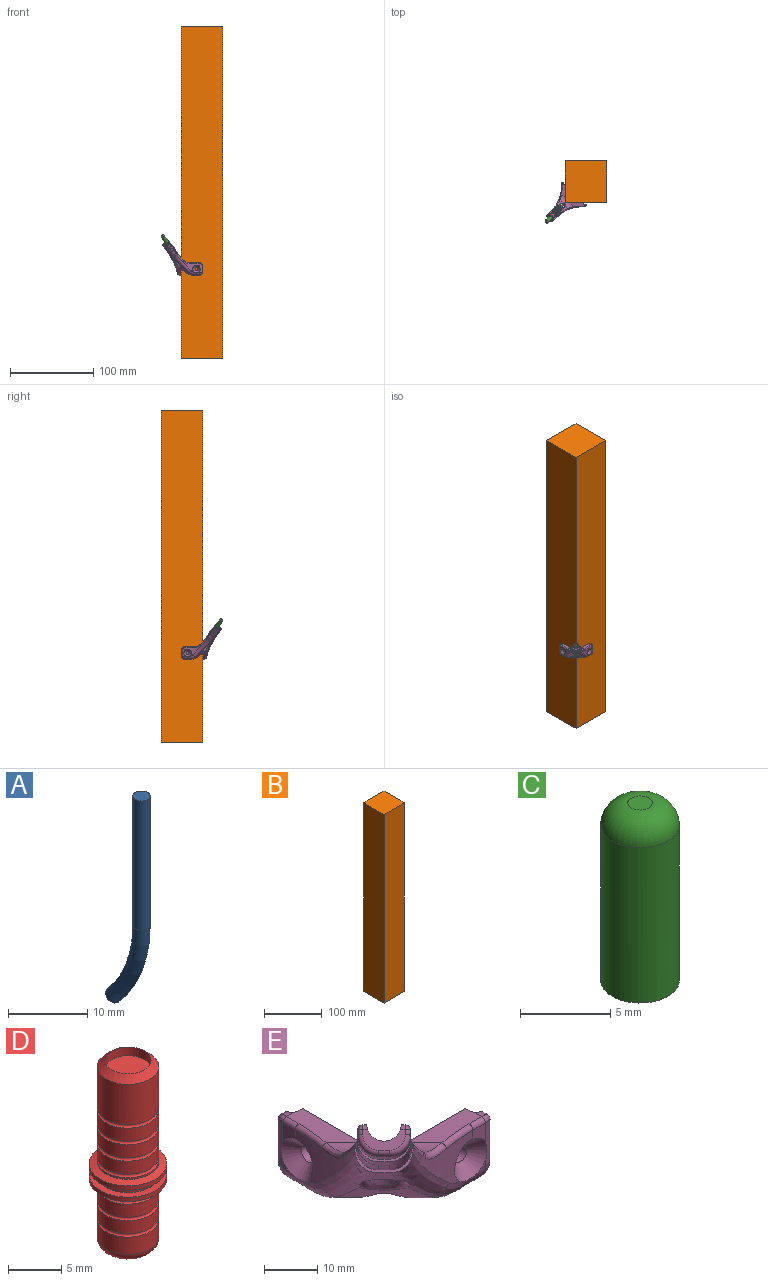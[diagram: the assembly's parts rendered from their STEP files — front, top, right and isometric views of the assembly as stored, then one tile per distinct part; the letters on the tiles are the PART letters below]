
ASSEMBLY  parts=5 mates=6
PART A: 4 faces, bbox 2.2x8.7x35.1 mm
  f0: plane 2.2x2.2mm, normal (0,0,1), area 3.8mm2, adj f2
  f1: plane 2.2x1.65mm, normal (0,0.66,-0.75), area 3.8mm2, adj f3
  f2: cylinder r=1.1mm len=20mm, axis (0,0,-1), area 138.2mm2, adj f0,f3
  f3: torus R=20mm, axis (1,0,0), area 99.9mm2, adj f1,f2
PART B: 6 faces, bbox 50x50x400 mm
  f0: plane 400x50mm, normal (0,-1,0), area 20000mm2, adj f1,f3,f4,f5
  f1: plane 400x50mm, normal (1,0,0), area 20000mm2, adj f0,f2,f4,f5
  f2: plane 400x50mm, normal (0,1,0), area 20000mm2, adj f1,f3,f4,f5
  f3: plane 400x50mm, normal (-1,0,0), area 20000mm2, adj f0,f2,f4,f5
  f4: plane 50x50mm, normal (0,0,1), area 2500mm2, adj f0,f1,f2,f3
  f5: plane 50x50mm, normal (0,0,-1), area 2500mm2, adj f0,f1,f2,f3
PART C: 4 faces, bbox 4.4x4.4x12 mm
  f0: cylinder r=2.17mm len=10.5mm, axis (0,0,-1), area 143.5mm2, adj f2,f3
  f1: plane 1.35x1.35mm, normal (0,0,1), area 1.4mm2, adj f3
  f2: plane 4.35x4.35mm, normal (0,0,-1), area 14.9mm2, adj f0
  f3: torus R=0.68mm, axis (0,0,1), area 24.1mm2, adj f0,f1
PART D: 30 faces, bbox 7.3x7.3x21.3 mm
  f0: cylinder r=2.9mm len=5.8mm, axis (0,0,-1), area 3.6mm2, adj f2,f10
  f1: cylinder r=2.9mm len=5.8mm, axis (0,0,-1), area 3.6mm2, adj f8,f9
  f2: cone r=2.9mm half-angle=73.3deg, axis (0,0,1), area 16.1mm2, adj f0,f3
  f3: cylinder r=3.65mm len=7.3mm, axis (0,0,-1), area 11.5mm2, adj f2,f4
  f4: plane 7.3x7.3mm, normal (0,0,1), area 15.4mm2, adj f3,f5
  f5: cylinder r=2.9mm len=5.8mm, axis (0,0,-1), area 14.6mm2, adj f4,f6
  f6: plane 7.3x7.3mm, normal (0,0,-1), area 15.4mm2, adj f5,f7
  f7: cylinder r=3.65mm len=7.3mm, axis (0,0,-1), area 11.5mm2, adj f6,f8
  f8: cone r=3.65mm half-angle=73.3deg, axis (0,0,-1), area 16.1mm2, adj f1,f7
  f9: torus R=2.9mm, axis (0,0,1), area 10.9mm2, adj f1,f11
  f10: torus R=2.9mm, axis (0,0,1), area 10.9mm2, adj f0,f13
  f11: cylinder r=2.9mm len=5.8mm, axis (0,0,-1), area 27.3mm2, adj f9,f12
  f12: torus R=2.9mm, axis (0,0,1), area 10.9mm2, adj f11,f15
  f13: cylinder r=2.9mm len=5.8mm, axis (0,0,-1), area 27.3mm2, adj f10,f14
  f14: torus R=2.9mm, axis (0,0,1), area 10.9mm2, adj f13,f23
  f15: cylinder r=2.9mm len=5.8mm, axis (0,0,-1), area 27.3mm2, adj f12,f16
  f16: torus R=2.9mm, axis (0,0,1), area 10.9mm2, adj f15,f17
  f17: cylinder r=2.9mm len=5.8mm, axis (0,0,-1), area 27.3mm2, adj f16,f18
  f18: torus R=2.9mm, axis (0,0,1), area 10.9mm2, adj f17,f22
  f19: plane 4.35x4.35mm, normal (0,0,1), area 14.9mm2, adj f20
  f20: cylinder r=2.17mm len=4.35mm, axis (0,0,1), area 13.7mm2, adj f19,f21
  f21: cone r=2.9mm half-angle=45deg, axis (0,0,-1), area 16.3mm2, adj f20,f22
  f22: cylinder r=2.9mm len=5.8mm, axis (0,0,-1), area 84.3mm2, adj f18,f21
  f23: cylinder r=2.9mm len=5.8mm, axis (0,0,-1), area 27.3mm2, adj f14,f24
  f24: torus R=2.9mm, axis (0,0,1), area 10.9mm2, adj f23,f26
  f25: plane 3.8x3.8mm, normal (0,0,-1), area 6.4mm2, adj f27,f28
  f26: cylinder r=2.9mm len=5.8mm, axis (0,0,-1), area 36.4mm2, adj f24,f27
  f27: torus R=1.9mm, axis (0,0,-1), area 25mm2, adj f25,f26
  f28: cylinder r=1.25mm len=3mm, axis (0,0,-1), area 23.6mm2, adj f25,f29
  f29: plane 2.5x2.5mm, normal (0,0,-1), area 4.9mm2, adj f28
PART E: 96 faces, bbox 50.5x50.5x41 mm
  f0: cylinder r=3mm len=10mm, axis (0,0,-1), area 35.9mm2, adj f27,f28,f71,f72,f73,f95
  f1: cylinder r=3mm len=2.91mm, axis (1,0,0), area 4.6mm2, adj f2,f37,f88,f91,f92,f93
  f2: bspline ~3.11x2.67mm, area 4.9mm2, adj f1,f30,f51,f92
  f3: cylinder r=1.25mm len=14.99mm, axis (0,0,1), area 40.8mm2, adj f4,f6,f70,f72,f87,f94
  f4: cylinder r=4mm len=4mm, axis (1,0,0), area 19.8mm2, adj f3,f5,f21,f28,f72,f73,f87
  f5: plane 6.68x1.07mm, normal (0,0,-1), area 6.2mm2, adj f4,f21,f38,f41,f87
  f6: plane 16.14x4.79mm, normal (0,0,1), area 58.5mm2, adj f3,f34,f38,f55,f56,f70,f87
  f7: plane 20.85x16.08mm, normal (1,0,0), area 270.2mm2, adj f20,f34,f36,f37,f42,f68,f76,f89
  f8: plane 6.92x6.92mm, normal (-0.5,-0.5,-0.71), area 28.8mm2, adj f13,f14,f80,f86
  f9: cylinder r=40mm len=24.02mm, axis (0,0,-1), area 92mm2, adj f13,f16,f22,f27,f56,f57,f78,f86
  f10: cylinder r=40mm len=5.65mm, axis (0,0,-1), area 6.9mm2, adj f16,f40,f49,f84,f85
  f11: cylinder r=40mm len=24.02mm, axis (0,0,-1), area 92mm2, adj f14,f15,f24,f25,f52,f53,f77,f86
  f12: cylinder r=40mm len=5.65mm, axis (0,0,-1), area 6.9mm2, adj f15,f39,f50,f84,f85
  f13: bspline ~21.97x21.5mm, area 143.1mm2, adj f8,f9,f20,f22,f80,f86
  f14: bspline ~21.97x21.5mm, area 143.1mm2, adj f8,f11,f20,f24,f80,f86
  f15: bspline ~15.71x12.85mm, area 35.9mm2, adj f11,f12,f33,f53,f54,f85,f86
  f16: bspline ~15.71x12.85mm, area 35.9mm2, adj f9,f10,f32,f57,f58,f85,f86
  f17: plane 6.36x6.03mm, normal (-0.5,-0.5,-0.71), area 18.6mm2, adj f18,f19,f49,f50,f82,f84
  f18: cylinder r=4mm len=9.65mm, axis (-0.5,-0.5,0.71), area 42.5mm2, adj f17,f31,f40,f49,f62,f81,f82,f83
  f19: cylinder r=4mm len=9.65mm, axis (0.5,0.5,-0.71), area 42.5mm2, adj f17,f31,f39,f50,f64,f81,f82,f83
  f20: plane 15.74x15.74mm, normal (-0.5,-0.5,-0.71), area 101.7mm2, adj f7,f13,f14,f38,f41,f42,f68,f80
  f21: torus R=44mm, axis (0,0,1), area 12.8mm2, adj f4,f5,f22,f73,f78
  f22: bspline ~10.48x7.01mm, area 37.5mm2, adj f9,f13,f21,f41,f78
  f23: torus R=44mm, axis (0,0,1), area 12.8mm2, adj f24,f29,f36,f75,f77
  f24: bspline ~10.95x7.07mm, area 37.5mm2, adj f11,f14,f23,f42,f77
  f25: plane 4.44x3.36mm, normal (-1,0,0), area 9.5mm2, adj f11,f30,f51,f75
  f26: plane 1.44x1.17mm, normal (-1,0,0), area 0.7mm2, adj f29,f30,f75
  f27: plane 4.44x3.36mm, normal (0,-1,0), area 9.5mm2, adj f0,f9,f55,f73
  f28: plane 1.44x1.17mm, normal (0,-1,0), area 0.7mm2, adj f0,f4,f73
  f29: cylinder r=4mm len=4mm, axis (0,-1,0), area 19.8mm2, adj f23,f26,f36,f69,f75,f88,f89
  f30: cylinder r=3mm len=10mm, axis (0,0,-1), area 35.5mm2, adj f2,f25,f26,f69,f75,f92
  f31: plane 2.91x2.91mm, normal (-0.5,-0.5,-0.71), area 6mm2, adj f18,f19,f63,f83
  f32: plane 21.26x17.62mm, normal (0.5,0.5,0.71), area 41.7mm2, adj f16,f34,f43,f44,f45,f46,f47,f48
  f33: plane 21.26x17.62mm, normal (0.5,0.5,0.71), area 41.7mm2, adj f15,f34,f43,f44,f45,f46,f47,f48
  f34: cylinder r=10mm len=20.43mm, axis (0.71,-0.71,0), area 119.8mm2, adj f6,f7,f32,f33,f37,f38,f48,f53
  f35: plane 6.63x6.63mm, normal (-0.5,-0.5,0.71), area 17.9mm2, adj f43,f59,f61,f62,f63,f64,f65,f67
  f36: plane 6.68x1.07mm, normal (0,0,-1), area 6.2mm2, adj f7,f23,f29,f42,f89
  f37: plane 16.14x4.79mm, normal (0,0,1), area 58.5mm2, adj f1,f7,f34,f51,f52,f88,f89
  f38: plane 20.85x16.08mm, normal (0,1,0), area 270.2mm2, adj f5,f6,f20,f34,f41,f68,f74,f87
  f39: plane 7.52x4.82mm, normal (-0.71,0.71,0), area 9.1mm2, adj f12,f19,f54,f65
  f40: plane 7.52x4.82mm, normal (0.71,-0.71,0), area 9.1mm2, adj f10,f18,f58,f61
  f41: cylinder r=10mm len=11.07mm, axis (0.71,-0.71,0), area 26.5mm2, adj f5,f20,f22,f38
  f42: cylinder r=10mm len=11.07mm, axis (0.71,-0.71,0), area 26.5mm2, adj f7,f20,f24,f36
  f43: cylinder r=3.25mm len=10.61mm, axis (-0.5,-0.5,0.71), area 111.3mm2, adj f32,f33,f35,f46,f59,f67
  f44: cylinder r=3.75mm len=7.15mm, axis (-0.5,-0.5,0.71), area 29.5mm2, adj f32,f33,f45,f46
  f45: plane 5.9x5.9mm, normal (-0.5,-0.5,0.71), area 5.5mm2, adj f32,f33,f44,f47
  f46: plane 5.9x5.9mm, normal (0.5,0.5,-0.71), area 5.5mm2, adj f32,f33,f43,f44
  f47: cylinder r=3.25mm len=12.9mm, axis (-0.5,-0.5,0.71), area 153.2mm2, adj f32,f33,f45,f79
  f48: extruded ~9.96x5.62mm, area 75.6mm2, adj f32,f33,f34,f79,f80
  f49: bspline ~18.12x15.11mm, area 32.9mm2, adj f10,f17,f18,f84
  f50: bspline ~18.12x15.11mm, area 32.9mm2, adj f12,f17,f19,f84
  f51: cylinder r=1mm len=3.36mm, axis (0,1,0), area 5.3mm2, adj f2,f25,f37,f52
  f52: torus R=41mm, axis (0,0,1), area 12.4mm2, adj f11,f37,f51,f53
  f53: bspline ~11.37x5.78mm, area 15.5mm2, adj f11,f15,f34,f52
  f54: cylinder r=1mm len=6.82mm, axis (-0.5,-0.5,0.71), area 13.6mm2, adj f15,f33,f39,f66
  f55: cylinder r=1mm len=3.36mm, axis (-1,0,0), area 5.3mm2, adj f6,f27,f56,f71
  f56: torus R=41mm, axis (0,0,1), area 12.4mm2, adj f6,f9,f55,f57
  f57: bspline ~11.37x5.78mm, area 15.5mm2, adj f9,f16,f34,f56
  f58: cylinder r=1mm len=6.82mm, axis (0.5,0.5,-0.71), area 13.6mm2, adj f16,f32,f40,f60
  f59: cylinder r=1mm len=1.64mm, axis (0.71,-0.71,0), area 1.3mm2, adj f32,f35,f43,f60
  f60: sphere r=1mm, area 1mm2, adj f58,f59,f61
  f61: cylinder r=1mm len=1.71mm, axis (0.5,0.5,0.71), area 1.6mm2, adj f35,f40,f60,f62
  f62: torus R=3mm, axis (0.5,0.5,-0.71), area 9mm2, adj f18,f35,f61,f63
  f63: cylinder r=1mm len=1.62mm, axis (0.71,-0.71,0), area 3.1mm2, adj f31,f35,f62,f64
  f64: torus R=3mm, axis (0.5,0.5,-0.71), area 9mm2, adj f19,f35,f63,f65
  f65: cylinder r=1mm len=1.71mm, axis (-0.5,-0.5,-0.71), area 1.6mm2, adj f35,f39,f64,f66
  f66: sphere r=1mm, area 1.6mm2, adj f54,f65,f67
  f67: cylinder r=1mm len=1.64mm, axis (0.71,-0.71,0), area 1.3mm2, adj f33,f35,f43,f66
  f68: cylinder r=1.5mm len=10.03mm, axis (0,0,1), area 23.6mm2, adj f7,f20,f34,f38
  f69: torus R=1mm, axis (0,1,0), area 14.8mm2, adj f29,f30,f88,f91,f92,f93
  f70: cylinder r=3mm len=2.91mm, axis (0,-1,0), area 4.6mm2, adj f3,f6,f71,f90,f94,f95
  f71: bspline ~3.11x2.67mm, area 4.9mm2, adj f0,f55,f70,f95
  f72: torus R=1mm, axis (1,0,0), area 14.8mm2, adj f0,f3,f4,f90,f94,f95
  f73: cone r=1.8mm half-angle=45deg, axis (0,-1,0), area 75.2mm2, adj f0,f4,f21,f27,f28,f74,f78
  f74: cylinder r=1.8mm len=3.6mm, axis (0,-1,0), area 26mm2, adj f38,f73
  f75: cone r=1.8mm half-angle=45deg, axis (-1,0,0), area 75.3mm2, adj f23,f25,f26,f29,f30,f76,f77
  f76: cylinder r=1.8mm len=3.6mm, axis (-1,0,0), area 26mm2, adj f7,f75
  f77: extruded ~8.7x5.14mm, area 2.4mm2, adj f11,f23,f24,f75
  f78: extruded ~8.7x5.14mm, area 2.4mm2, adj f9,f21,f22,f73
  f79: bspline ~5.39x5.39mm, area 4.2mm2, adj f47,f48,f80
  f80: bspline ~10x9.62mm, area 87.1mm2, adj f8,f13,f14,f20,f48,f79
  f81: cylinder r=5.5mm len=8.64mm, axis (-0.5,-0.5,0.71), area 37.5mm2, adj f18,f19,f82,f83
  f82: plane 7.56x7.56mm, normal (-0.5,-0.5,0.71), area 7.5mm2, adj f17,f18,f19,f81
  f83: plane 7.56x7.56mm, normal (0.5,0.5,-0.71), area 7.5mm2, adj f18,f19,f31,f81
  f84: plane 8.22x8.22mm, normal (0.5,0.5,-0.71), area 8.9mm2, adj f10,f12,f17,f49,f50,f85
  f85: cylinder r=5.5mm len=9.81mm, axis (-0.5,-0.5,0.71), area 44.6mm2, adj f10,f12,f15,f16,f84,f86
  f86: plane 9.19x9.19mm, normal (-0.5,-0.5,0.71), area 11.3mm2, adj f8,f9,f11,f13,f14,f15,f16,f85
  f87: plane 15x1.25mm, normal (1,0,0), area 18.7mm2, adj f3,f4,f5,f6,f38
  f88: cylinder r=1.25mm len=14.99mm, axis (0,0,1), area 40.8mm2, adj f1,f29,f37,f69,f89,f93
  f89: plane 15x1.25mm, normal (0,1,0), area 18.7mm2, adj f7,f29,f36,f37,f88
  f90: plane 13.07x0.33mm, normal (0,1,0), area 4mm2, adj f70,f72,f94,f95
  f91: plane 13.07x0.33mm, normal (1,0,0), area 4mm2, adj f1,f69,f92,f93
  f92: cylinder r=0.5mm len=12.3mm, axis (0,0,-1), area 9.4mm2, adj f1,f2,f30,f69,f91
  f93: cylinder r=0.5mm len=13.58mm, axis (0,0,1), area 4.6mm2, adj f1,f69,f88,f91
  f94: cylinder r=0.5mm len=13.58mm, axis (0,0,1), area 4.6mm2, adj f3,f70,f72,f90
  f95: cylinder r=0.5mm len=12.3mm, axis (0,0,-1), area 9.4mm2, adj f0,f70,f71,f72,f90
PLACE A rot(axis=(-0.16,-0.37,0.91),140.8deg) t=(-36.4,-36.4,130.61)mm
PLACE B at identity
PLACE C rot(axis=(0.47,0.04,-0.88),106.9deg) t=(-32.15,-32.15,124.6)mm
PLACE D rot(axis=(-0.16,-0.37,0.91),140.8deg) t=(-32.15,-32.15,124.6)mm
PLACE E t=(-25,-25,99.5)mm
MATE cylindrical C.f0 <-> D.f0  axis (0.5,0.5,-0.71) through (-42.3,-42.3,138.96)mm
MATE planar B.f0 <-> E.f38  axis (0,-1,0) through (0,-25,200)mm
MATE planar E.f7 <-> B.f3  axis (1,0,0) through (-25,-13.03,107.54)mm
MATE planar D.f0 <-> C.f0  axis (-0.5,-0.5,0.71) through (-42.3,-42.3,138.96)mm
MATE cylindrical C.f0 <-> E.f47  axis (0.5,0.5,-0.71) through (-44.92,-44.92,142.67)mm
MATE fastened A.f2 <-> D.f28  axis (0.5,0.5,-0.71) through (-32.9,-32.9,125.66)mm
